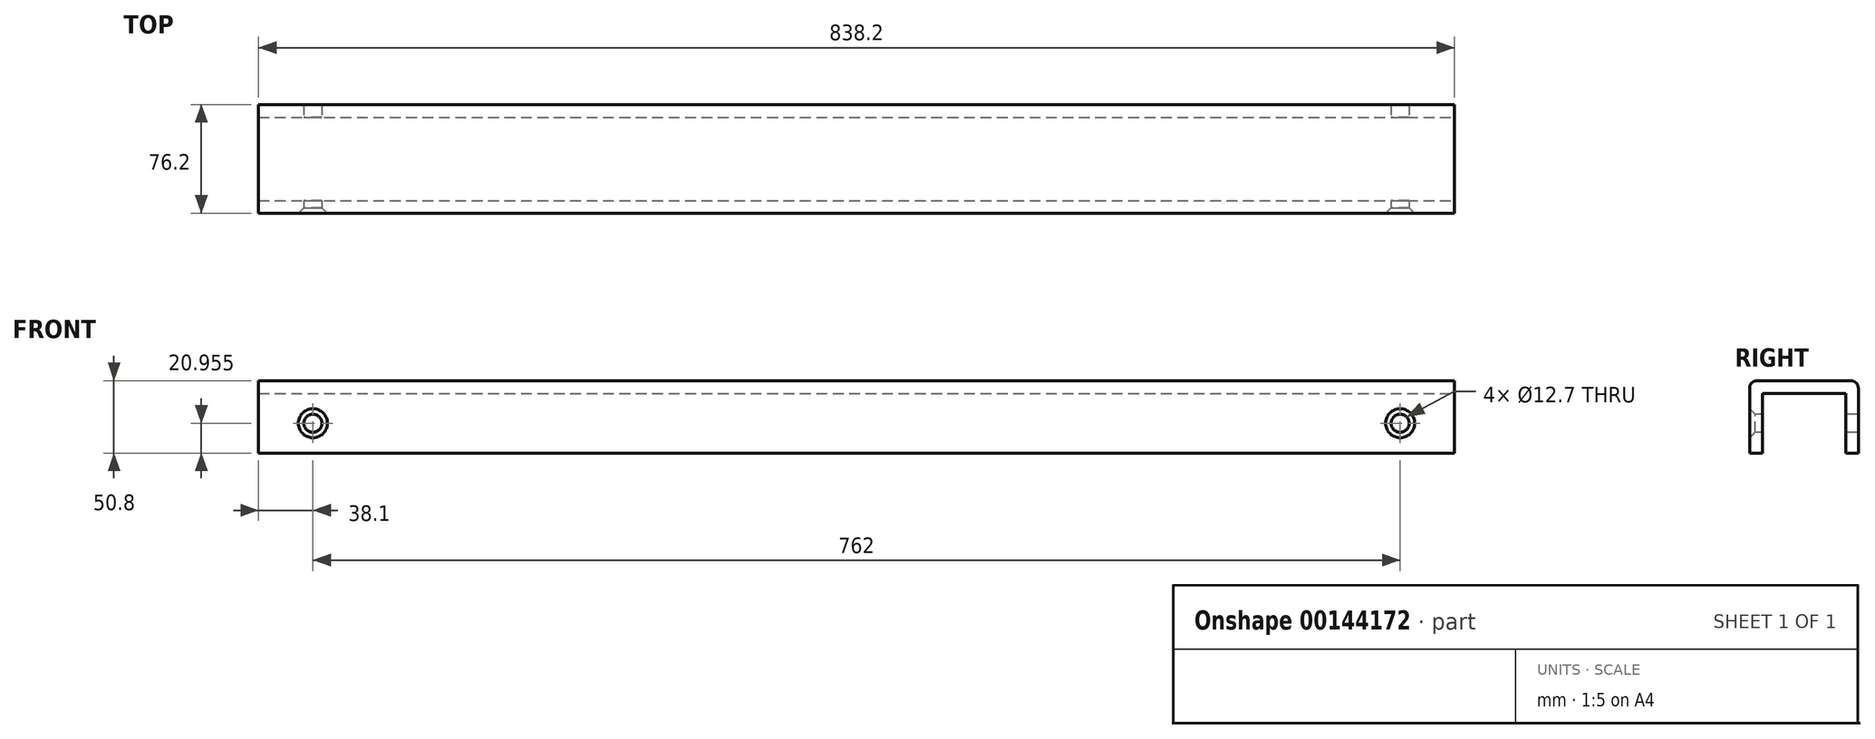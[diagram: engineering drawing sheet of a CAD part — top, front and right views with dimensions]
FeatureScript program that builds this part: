
annotation { "Feature Type Name" : "Feature", "Feature Type Description" : "" }
export const myFeature = defineFeature(function(context is Context, id is Id, definition is map)
    precondition{}
    {
        {
            var Q0;
            Q0=qCreatedBy(makeId("Front.planeOp"),FACE);
            var sketch = newSketch(context, id + "F0", { "sketchPlane" : qUnion([Q0])});
            skLineSegment(sketch, "E0", {"start": v(0, 0) * mm, "end": v(838.2, 0) * mm});
            skLineSegment(sketch, "E1", {"start": v(838.2, 0) * mm, "end": v(838.2, -50.8) * mm});
            skLineSegment(sketch, "E2", {"start": v(0, 0) * mm, "end": v(0, -50.8) * mm});
            skLineSegment(sketch, "E3", {"start": v(0, -50.8) * mm, "end": v(838.2, -50.8) * mm});
            skSolve(sketch);
        }
        {
            var Q0;
            Q0=makeQuery(id+"F0.imprint","IMPRINT",FACE,{"disambiguationData":[TD([[makeQuery(id+"F0.imprint","IMPRINT",EDGE,{"derivedFrom":sQuery(id+"F0.wireOp",EDGE,"E0")}),-1.0]])]});
            extrude(context, id + "F1", {"entities" : qUnion([Q0]), "depth" : 76.2 * mm});
        }
        {
            var Q0;
            Q0=makeQuery(id+"F1.opExtrude","CAP_FACE",FACE,{"disambiguationData":[OSD([sQuery(id+"F0.wireOp",EDGE,"E0"),sQuery(id+"F0.wireOp",EDGE,"E1"),sQuery(id+"F0.wireOp",EDGE,"E2"),sQuery(id+"F0.wireOp",EDGE,"E3")])],"isStart":false});
            var sketch = newSketch(context, id + "F2", { "sketchPlane" : qUnion([Q0])});
            skPoint(sketch, "E4", {"position": v(38.1, -29.85) * mm});
            skPoint(sketch, "E5", {"position": v(800.1, -29.84) * mm});
            skSolve(sketch);
        }
        {
            var Q0;
            Q0=makeQuery(id+"F1.opExtrude","SWEPT_FACE",FACE,{"disambiguationData":[OSD([sQuery(id+"F0.wireOp",EDGE,"E1")])]});
            var Q1;
            Q1=makeQuery(id+"F1.opExtrude","SWEPT_FACE",FACE,{"disambiguationData":[OSD([sQuery(id+"F0.wireOp",EDGE,"E3")])]});
            var Q2;
            Q2=makeQuery(id+"F1.opExtrude","SWEPT_FACE",FACE,{"disambiguationData":[OSD([sQuery(id+"F0.wireOp",EDGE,"E2")])]});
            shell(context, id + "F3", {"entities" : qUnion([Q0, Q1, Q2]), "thickness" : 8.9 * mm});
        }
        {
            var Q0;
            Q0=sQuery(id+"F2.wireOp",VERTEX,"E4");
            var Q1;
            Q1=sQuery(id+"F2.wireOp",VERTEX,"E5");
            var Q2;
            Q2=makeQuery(id+"F1.opExtrude","SWEPT_BODY",BODY,{"disambiguationData":[OSD([sQuery(id+"F0.wireOp",EDGE,"E0"),sQuery(id+"F0.wireOp",EDGE,"E1"),sQuery(id+"F0.wireOp",EDGE,"E2"),sQuery(id+"F0.wireOp",EDGE,"E3")])]});
            hole(context, id + "F4", {"style" : HoleStyle.C_SINK, "endStyle" : HoleEndStyle.THROUGH, "holeDiameter" : 12.7 * mm, "cSinkDiameter" : 20.32 * mm, "cSinkAngle" : 90 * degree, "locations" : qUnion([Q0, Q1]), "scope" : qUnion([Q2]), "isTappedThrough" : true});
        }
        {
            var Q0;
            Q0=makeQuery(id+"F1.opExtrude","CAP_EDGE",EDGE,{"disambiguationData":[OSD([sQuery(id+"F0.wireOp",EDGE,"E0")])],"isStart":false});
            var Q1;
            Q1=makeQuery(id+"F1.opExtrude","CAP_EDGE",EDGE,{"disambiguationData":[OSD([sQuery(id+"F0.wireOp",EDGE,"E0")])],"isStart":true});
            fillet(context, id + "F5", {"entities" : qUnion([Q0, Q1]), "radius" : 5.08 * mm, "tangentPropagation" : true, "allowEdgeOverflow" : false});
        }
    });
